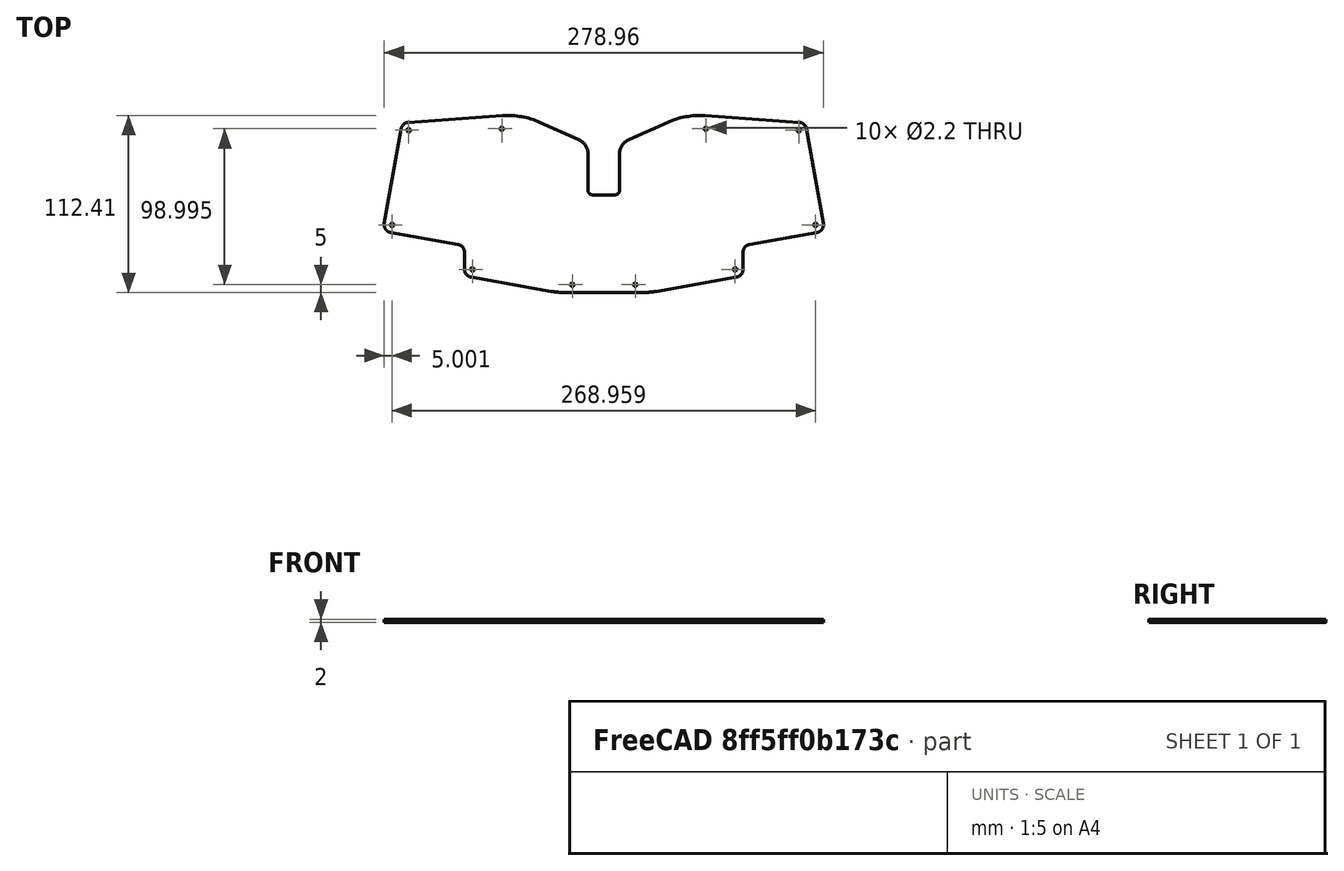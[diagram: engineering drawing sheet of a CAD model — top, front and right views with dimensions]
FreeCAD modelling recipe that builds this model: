
FCSTD DOCUMENT  (FreeCAD 0.20R)
Label: Base-plate
License: All rights reserved
LicenseURL: http://en.wikipedia.org/wiki/All_rights_reserved
objects: Sketcher::SketchObject×1, PartDesign::Pad×1, PartDesign::Body×1
note: 4 computed .brp shape members not serialized (recipe doc carries the construction recipe); baked Part::Feature solids carry a one-line shape summary decoded from their .brp

FEATURE [Sketcher::SketchObject] Sketch
  FullyConstrained = false
  sketch-geometry (42):
    g0: ArcOfCircle CenterX=-123.886 CenterY=41.0758 CenterZ=0 NormalX=0 NormalY=0 NormalZ=1 AngleXU=0 Radius=5 StartAngle=1.64124 EndAngle=2.96706
    g1: LineSegment StartX=-128.81 StartY=41.944 StartZ=0 EndX=-139.403 EndY=-18.1331 EndZ=0
    g2: ArcOfCircle CenterX=-134.479 CenterY=-19.0013 CenterZ=0 NormalX=0 NormalY=0 NormalZ=1 AngleXU=0 Radius=5 StartAngle=2.96706 EndAngle=4.53786
    g3: LineSegment StartX=-135.348 StartY=-23.9254 StartZ=0 EndX=-92.5693 EndY=-31.4683 EndZ=0
    g4: ArcOfCircle CenterX=-93.4375 CenterY=-36.3924 CenterZ=0 NormalX=0 NormalY=0 NormalZ=1 AngleXU=0 Radius=5 StartAngle=0 EndAngle=1.39626
    g5: LineSegment StartX=-88.4375 StartY=-36.3924 StartZ=0 EndX=-88.4375 EndY=-47.3453 EndZ=0
    g6: ArcOfCircle CenterX=-83.4375 CenterY=-47.3453 CenterZ=0 NormalX=0 NormalY=0 NormalZ=1 AngleXU=0 Radius=5 StartAngle=3.14159 EndAngle=4.53786
    g7: LineSegment StartX=-124.238 StartY=46.0634 StartZ=0 EndX=-64.3588 EndY=50.2886 EndZ=0
    g8: ArcOfCircle CenterX=-60.8394 CenterY=0.412619 CenterZ=0 NormalX=0 NormalY=0 NormalZ=1 AngleXU=0 Radius=50 StartAngle=1.15128 EndAngle=1.64124
    g9: LineSegment StartX=-84.3057 StartY=-52.2693 StartZ=0 EndX=-33.4282 EndY=-61.2404 EndZ=0
    g10: ArcOfCircle CenterX=-24.7458 CenterY=-12 CenterZ=0 NormalX=0 NormalY=0 NormalZ=1 AngleXU=0 Radius=50 StartAngle=4.53786 EndAngle=4.71239
    g11: ArcOfCircle CenterX=123.886 CenterY=41.0758 CenterZ=0 NormalX=0 NormalY=0 NormalZ=1 AngleXU=0 Radius=5 StartAngle=0.174533 EndAngle=1.50035
    g12: LineSegment StartX=128.81 StartY=41.944 StartZ=0 EndX=139.403 EndY=-18.1331 EndZ=0
    g13: ArcOfCircle CenterX=134.479 CenterY=-19.0013 CenterZ=0 NormalX=0 NormalY=0 NormalZ=1 AngleXU=0 Radius=5 StartAngle=4.88692 EndAngle=6.45772
    g14: LineSegment StartX=135.348 StartY=-23.9254 StartZ=0 EndX=92.5693 EndY=-31.4683 EndZ=0
    g15: ArcOfCircle CenterX=93.4375 CenterY=-36.3924 CenterZ=0 NormalX=0 NormalY=0 NormalZ=1 AngleXU=0 Radius=5 StartAngle=1.74533 EndAngle=3.14159
    g16: LineSegment StartX=88.4375 StartY=-36.3924 StartZ=0 EndX=88.4375 EndY=-47.3453 EndZ=0
    g17: ArcOfCircle CenterX=83.4375 CenterY=-47.3453 CenterZ=0 NormalX=0 NormalY=0 NormalZ=1 AngleXU=0 Radius=5 StartAngle=4.88692 EndAngle=6.28319
    g18: LineSegment StartX=124.238 StartY=46.0634 StartZ=0 EndX=64.3588 EndY=50.2886 EndZ=0
    g19: ArcOfCircle CenterX=60.8394 CenterY=0.412619 CenterZ=0 NormalX=0 NormalY=0 NormalZ=1 AngleXU=0 Radius=50 StartAngle=1.50035 EndAngle=1.99031
    g20: LineSegment StartX=84.3057 StartY=-52.2693 StartZ=0 EndX=33.4282 EndY=-61.2404 EndZ=0
    g21: ArcOfCircle CenterX=24.7458 CenterY=-12 CenterZ=0 NormalX=0 NormalY=0 NormalZ=1 AngleXU=0 Radius=50 StartAngle=4.71239 EndAngle=4.88692
    g22: LineSegment StartX=-24.7458 StartY=-62 StartZ=0 EndX=24.7458 EndY=-62 EndZ=0
    g23: LineSegment StartX=40.4737 StartY=46.077 StartZ=0 EndX=15.9269 EndY=35.1294 EndZ=0
    g24: LineSegment StartX=-40.4737 StartY=46.077 StartZ=0 EndX=-15.9269 EndY=35.1294 EndZ=0
    g25: ArcOfCircle CenterX=7 CenterY=3 CenterZ=0 NormalX=0 NormalY=0 NormalZ=1 AngleXU=0 Radius=3 StartAngle=4.71239 EndAngle=6.28319
    g26: LineSegment StartX=-7 StartY=0 StartZ=0 EndX=7 EndY=0 EndZ=0
    g27: ArcOfCircle CenterX=-7 CenterY=3 CenterZ=0 NormalX=0 NormalY=0 NormalZ=1 AngleXU=0 Radius=3 StartAngle=3.14159 EndAngle=4.71239
    g28: LineSegment StartX=10 StartY=3 StartZ=0 EndX=10 EndY=25.9966 EndZ=0
    g29: LineSegment StartX=-10 StartY=3 StartZ=0 EndX=-10 EndY=25.9966 EndZ=0
    g30: ArcOfCircle CenterX=20 CenterY=25.9966 CenterZ=0 NormalX=0 NormalY=0 NormalZ=1 AngleXU=0 Radius=10 StartAngle=1.99031 EndAngle=3.14159
    g31: ArcOfCircle CenterX=-20 CenterY=25.9966 CenterZ=0 NormalX=0 NormalY=0 NormalZ=1 AngleXU=0 Radius=10 StartAngle=0 EndAngle=1.15128
    g32: Circle CenterX=123.886 CenterY=41.0758 CenterZ=0 NormalX=0 NormalY=0 NormalZ=-1 AngleXU=0 Radius=1.1
    g33: Circle CenterX=134.479 CenterY=-19.0013 CenterZ=0 NormalX=0 NormalY=0 NormalZ=-1 AngleXU=0 Radius=1.1
    g34: Circle CenterX=83.4375 CenterY=-47.3453 CenterZ=0 NormalX=0 NormalY=0 NormalZ=-1 AngleXU=0 Radius=1.1
    g35: Circle CenterX=20 CenterY=-57 CenterZ=0 NormalX=0 NormalY=0 NormalZ=-1 AngleXU=0 Radius=1.1
    g36: Circle CenterX=-20 CenterY=-57 CenterZ=0 NormalX=0 NormalY=0 NormalZ=-1 AngleXU=0 Radius=1.1
    g37: Circle CenterX=-83.4375 CenterY=-47.3453 CenterZ=0 NormalX=0 NormalY=0 NormalZ=-1 AngleXU=0 Radius=1.1
    g38: Circle CenterX=-134.479 CenterY=-19.0013 CenterZ=0 NormalX=0 NormalY=0 NormalZ=-1 AngleXU=0 Radius=1.1
    g39: Circle CenterX=-64.77 CenterY=41.995 CenterZ=0 NormalX=0 NormalY=0 NormalZ=-1 AngleXU=0 Radius=1.1
    g40: Circle CenterX=-123.886 CenterY=41.0758 CenterZ=0 NormalX=0 NormalY=0 NormalZ=-1 AngleXU=0 Radius=1.1
    g41: Circle CenterX=64.77 CenterY=41.995 CenterZ=0 NormalX=0 NormalY=0 NormalZ=-1 AngleXU=0 Radius=1.1
FEATURE [PartDesign::Pad] Pad
  Direction = (0,0,1)
  Length = 2
  Length2 = 10
  Profile = -> Sketch
  ReferenceAxis = -> Sketch [N_Axis]
  Type = 0
FEATURE [PartDesign::Body] Body  label="Plate"
  Group = -> [Sketch,Pad]
  Origin = -> Origin
  Tip = -> Pad
